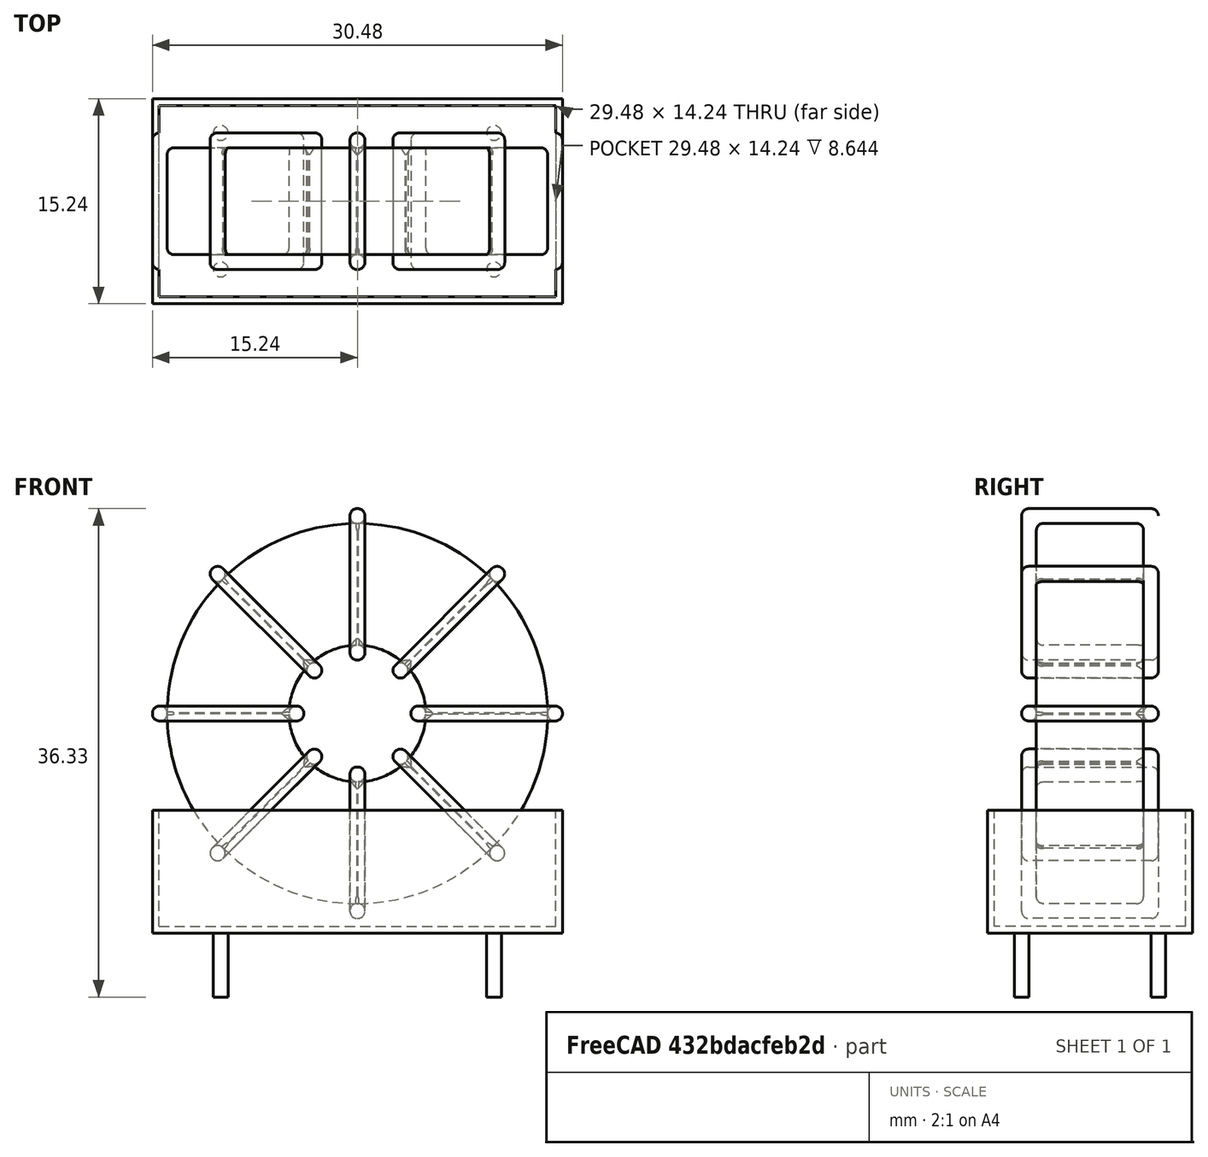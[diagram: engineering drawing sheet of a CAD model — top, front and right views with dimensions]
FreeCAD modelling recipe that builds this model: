
FCSTD DOCUMENT  (FreeCAD 0.16R6712 (Git))
Label: L_CommonMode_Toroid_Vertical_L30.5mm_W15.2mm_Px10.16mm_Py20.32mm_Bourns_8100
License: All rights reserved
LicenseURL: http://en.wikipedia.org/wiki/All_rights_reserved
objects: Sketcher::SketchObject×8, PartDesign::Pad×8, PartDesign::Fillet×5, Spreadsheet::Sheet×1, Part::MultiFuse×1
note: 30 computed .brp shape members not serialized (recipe doc carries the construction recipe); baked Part::Feature solids carry a one-line shape summary decoded from their .brp

FEATURE [Spreadsheet::Sheet] Spreadsheet  label="dimensions"
  cells = A1=Wx; B1(Wx)=30.48; C1(WW)=10.16; D1(iWx)=30.48; A2=Wy; B2(Wy)=10.16; D2(iWy)=15.24; A3=RM; B3(RMx)=10.16; C3(RMy)=20.32; A4=d_wire; B4(d_wire)=1.1; A5=H; B5(H)=31; A6=offsetx; B6(offsetx)=5.079999999999998
FEATURE [Sketcher::SketchObject] Sketch
  Placement = pos=(10.16,-5.08,0) rot=(1,0,0;1.5708rad)
  expr: Placement.Base.x = Spreadsheet.RMy / 2
  expr: Constraints[4] = Spreadsheet.WW / 2
  expr: Placement.Base.y = -Spreadsheet.RMx / 2
  expr: Constraints[0] = Spreadsheet.Wx / 2 - Spreadsheet.d_wire
  expr: Constraints[2] = Spreadsheet.Wx / 2 + Spreadsheet.d_wire + 0.5
  sketch-geometry (2):
    g0: Circle CenterX=0 CenterY=16.84 CenterZ=0 NormalX=0 NormalY=0 NormalZ=1 Radius=14.14
    g1: Circle CenterX=0 CenterY=16.84 CenterZ=0 NormalX=0 NormalY=0 NormalZ=1 Radius=5.08
  constraints (5):
    c: Radius(g0) = 14.14
    c: DistanceX(g-1,g0) = 0
    c: DistanceY(g-1,g0) = 16.84
    c: Coincident(g1,g0)
    c: Radius(g1) = 5.08
FEATURE [PartDesign::Pad] Pad
  Length = 7.96
  Length2 = 100
  Midplane = true
  Placement = pos=(10.16,-5.08,0) rot=(1,0,0;1.5708rad)
  Sketch = -> Sketch
  Type = 0
  expr: Length = Spreadsheet.Wy - 2 * Spreadsheet.d_wire
FEATURE [Sketcher::SketchObject] Sketch001
  Placement = pos=(0,0,0.75) rot=(0,0,1;0rad)
  expr: Constraints[4] = Spreadsheet.RMy
  expr: Constraints[2] = -Spreadsheet.RMx
  expr: Constraints[1] = Spreadsheet.d_wire / 2
  sketch-geometry (4):
    g0: Circle CenterX=0 CenterY=0 CenterZ=0 NormalX=0 NormalY=0 NormalZ=1 Radius=0.55
    g1: Circle CenterX=20.32 CenterY=-10.16 CenterZ=0 NormalX=0 NormalY=0 NormalZ=1 Radius=0.55
    g2: Circle CenterX=0 CenterY=-10.16 CenterZ=0 NormalX=0 NormalY=0 NormalZ=1 Radius=0.55
    g3: Circle CenterX=20.32 CenterY=0 CenterZ=0 NormalX=0 NormalY=0 NormalZ=1 Radius=0.55
  constraints (11):
    c: Equal(g0,g1)
    c: Radius(g0) = 0.55
    c: DistanceY(g-1,g1) = -10.16
    c: Coincident(g0,g-1)
    c: DistanceX(g-1,g1) = 20.32
    c: PointOnObject(g2,g-2)
    c: DistanceY(g-1,g3) = 0
    c: DistanceY(g2,g1) = 0
    c: DistanceX(g3,g1) = 0
    c: Equal(g3,g2)
    c: Equal(g2,g1)
FEATURE [PartDesign::Pad] Pad001
  Length = 5
  Length2 = 0
  Placement = pos=(0,0,0.75) rot=(0,0,1;0rad)
  Reversed = true
  Sketch = -> Sketch001
  Type = 0
FEATURE [PartDesign::Fillet] Fillet
  Base = -> Pad [Edge6,Edge3,Edge2]
  Placement = pos=(10.16,-5.08,0) rot=(1,0,0;1.5708rad)
  Radius = 0.5
FEATURE [Sketcher::SketchObject] Sketch003
  Placement = pos=(10.16,0,16.84) rot=(1,0,0;3.14159rad)
  expr: Placement.Base.x = Spreadsheet.RMy / 2
  expr: Constraints[18] = Spreadsheet.d_wire
  expr: Constraints[16] = Spreadsheet.d_wire
  expr: Constraints[19] = Spreadsheet.d_wire
  expr: Constraints[17] = Spreadsheet.d_wire
  expr: Placement.Base.y = -1 * (Spreadsheet.RMx - Spreadsheet.Wy) / 2
  expr: Constraints[21] = (Spreadsheet.Wx - Spreadsheet.WW) / 2 - Spreadsheet.d_wire
  expr: Constraints[22] = Spreadsheet.Wx / 2 - Spreadsheet.d_wire
  expr: Constraints[43] = Spreadsheet.d_wire
  expr: Constraints[48] = Spreadsheet.Wx - Spreadsheet.d_wire * 2
  expr: Constraints[49] = Spreadsheet.Wy
  expr: Placement.Base.z = Spreadsheet.Wx / 2 + Spreadsheet.d_wire + 0.5
  sketch-geometry (16):
    g0: LineSegment StartX=-3.98 StartY=0 StartZ=0 EndX=-15.24 EndY=0 EndZ=0
    g1: LineSegment StartX=-15.24 StartY=0 StartZ=0 EndX=-15.24 EndY=10.16 EndZ=0
    g2: LineSegment StartX=-15.24 StartY=10.16 StartZ=0 EndX=-3.98 EndY=10.16 EndZ=0
    g3: LineSegment StartX=-3.98 StartY=10.16 StartZ=0 EndX=-3.98 EndY=0 EndZ=0
    g4: LineSegment StartX=-14.14 StartY=9.06 StartZ=0 EndX=-5.08 EndY=9.06 EndZ=0
    g5: LineSegment StartX=-5.08 StartY=9.06 StartZ=0 EndX=-5.08 EndY=1.1 EndZ=0
    g6: LineSegment StartX=-5.08 StartY=1.1 StartZ=0 EndX=-14.14 EndY=1.1 EndZ=0
    g7: LineSegment StartX=-14.14 StartY=1.1 StartZ=0 EndX=-14.14 EndY=9.06 EndZ=0
    g8: LineSegment StartX=3.98 StartY=10.16 StartZ=0 EndX=15.24 EndY=10.16 EndZ=0
    g9: LineSegment StartX=15.24 StartY=10.16 StartZ=0 EndX=15.24 EndY=0 EndZ=0
    g10: LineSegment StartX=15.24 StartY=0 StartZ=0 EndX=3.98 EndY=0 EndZ=0
    g11: LineSegment StartX=3.98 StartY=0 StartZ=0 EndX=3.98 EndY=10.16 EndZ=0
    g12: LineSegment StartX=5.08 StartY=9.06 StartZ=0 EndX=14.14 EndY=9.06 EndZ=0
    g13: LineSegment StartX=14.14 StartY=9.06 StartZ=0 EndX=14.14 EndY=1.1 EndZ=0
    g14: LineSegment StartX=14.14 StartY=1.1 StartZ=0 EndX=5.08 EndY=1.1 EndZ=0
    g15: LineSegment StartX=5.08 StartY=1.1 StartZ=0 EndX=5.08 EndY=9.06 EndZ=0
  constraints (50):
    c: Horizontal(g0)
    c: Coincident(g1,g0)
    c: Vertical(g1)
    c: Coincident(g2,g1)
    c: Horizontal(g2)
    c: Coincident(g3,g2)
    c: Coincident(g3,g0)
    c: Vertical(g3)
    c: Coincident(g4,g5)
    c: Coincident(g5,g6)
    c: Coincident(g6,g7)
    c: Coincident(g7,g4)
    c: Horizontal(g4)
    c: Horizontal(g6)
    c: Vertical(g5)
    c: Vertical(g7)
    c: DistanceX(g1,g4) = 1.1
    c: DistanceY(g4,g1) = 1.1
    c: DistanceX(g5,g0) = 1.1
    c: DistanceY(g0,g5) = 1.1
    c: DistanceY(g-1,g0) = 0
    c: DistanceX(g6,g6) = 9.06
    c: DistanceX(g6,g-1) = 14.14
    c: Coincident(g8,g9)
    c: Coincident(g9,g10)
    c: Coincident(g10,g11)
    c: Coincident(g11,g8)
    c: Horizontal(g8)
    c: Horizontal(g10)
    c: Vertical(g9)
    c: Vertical(g11)
    c: Coincident(g12,g13)
    c: Coincident(g13,g14)
    c: Coincident(g14,g15)
    c: Coincident(g15,g12)
    c: Horizontal(g12)
    c: Horizontal(g14)
    c: Vertical(g13)
    c: Vertical(g15)
    c: DistanceY(g8,g2) = 0
    c: DistanceY(g10,g0) = 0
    c: DistanceY(g14,g5) = 0
    c: DistanceY(g12,g4) = 0
    c: DistanceX(g8,g12) = 1.1
    c: Equal(g8,g2)
    c: Equal(g12,g4)
    c: Equal(g9,g1)
    c: Equal(g13,g7)
    c: DistanceX(g4,g12) = 28.28
    c: DistanceY(g0,g1) = 10.16
FEATURE [PartDesign::Pad] Pad002
  Length = 1.1
  Length2 = 100
  Midplane = true
  Placement = pos=(10.16,0,16.84) rot=(1,0,0;3.14159rad)
  Sketch = -> Sketch003
  Type = 0
  expr: Length = Spreadsheet.d_wire
FEATURE [PartDesign::Fillet] Fillet001
  Base = -> Pad002 [Edge38,Edge41,Edge42,Edge43,Edge29,Edge32,Edge33,Edge34,Edge25,Edge35,Edge36,Edge13,Edge14,Edge15,Edge16,Edge17,Edge18,Edge19,Edge1,Edge2,Edge3,Edge4,Edge5,Edge6,Edge7,Edge37,Edge39,Edge40,Edge20,Edge23,Edge24,Edge21,Edge22,Edge8,Edge9,Edge10,Edge11,Edge12,Edge26,Edge27,+8 more]
  Placement = pos=(10.16,0,16.84) rot=(1,0,0;3.14159rad)
  Radius = 0.517
  expr: Radius = Spreadsheet.d_wire * 0.47
FEATURE [Sketcher::SketchObject] Sketch004
  Placement = pos=(10.16,0,16.84) rot=(0.92388,0,0.382683;3.14159rad)
  expr: Placement.Base.x = Spreadsheet.RMy / 2
  expr: Constraints[18] = Spreadsheet.d_wire
  expr: Constraints[16] = Spreadsheet.d_wire
  expr: Constraints[19] = Spreadsheet.d_wire
  expr: Constraints[17] = Spreadsheet.d_wire
  expr: Placement.Base.y = -1 * (Spreadsheet.RMx - Spreadsheet.Wy) / 2
  expr: Constraints[21] = (Spreadsheet.Wx - Spreadsheet.WW) / 2 - Spreadsheet.d_wire
  expr: Constraints[22] = Spreadsheet.Wx / 2 - Spreadsheet.d_wire
  expr: Constraints[43] = Spreadsheet.d_wire
  expr: Constraints[48] = Spreadsheet.Wx - 2 * Spreadsheet.d_wire
  expr: Constraints[49] = Spreadsheet.Wy
  expr: Placement.Base.z = Spreadsheet.Wx / 2 + Spreadsheet.d_wire + 0.5
  sketch-geometry (16):
    g0: LineSegment StartX=-3.98 StartY=0 StartZ=0 EndX=-15.24 EndY=0 EndZ=0
    g1: LineSegment StartX=-15.24 StartY=0 StartZ=0 EndX=-15.24 EndY=10.16 EndZ=0
    g2: LineSegment StartX=-15.24 StartY=10.16 StartZ=0 EndX=-3.98 EndY=10.16 EndZ=0
    g3: LineSegment StartX=-3.98 StartY=10.16 StartZ=0 EndX=-3.98 EndY=0 EndZ=0
    g4: LineSegment StartX=-14.14 StartY=9.06 StartZ=0 EndX=-5.08 EndY=9.06 EndZ=0
    g5: LineSegment StartX=-5.08 StartY=9.06 StartZ=0 EndX=-5.08 EndY=1.1 EndZ=0
    g6: LineSegment StartX=-5.08 StartY=1.1 StartZ=0 EndX=-14.14 EndY=1.1 EndZ=0
    g7: LineSegment StartX=-14.14 StartY=1.1 StartZ=0 EndX=-14.14 EndY=9.06 EndZ=0
    g8: LineSegment StartX=3.98 StartY=10.16 StartZ=0 EndX=15.24 EndY=10.16 EndZ=0
    g9: LineSegment StartX=15.24 StartY=10.16 StartZ=0 EndX=15.24 EndY=0 EndZ=0
    g10: LineSegment StartX=15.24 StartY=0 StartZ=0 EndX=3.98 EndY=0 EndZ=0
    g11: LineSegment StartX=3.98 StartY=0 StartZ=0 EndX=3.98 EndY=10.16 EndZ=0
    g12: LineSegment StartX=5.08 StartY=9.06 StartZ=0 EndX=14.14 EndY=9.06 EndZ=0
    g13: LineSegment StartX=14.14 StartY=9.06 StartZ=0 EndX=14.14 EndY=1.1 EndZ=0
    g14: LineSegment StartX=14.14 StartY=1.1 StartZ=0 EndX=5.08 EndY=1.1 EndZ=0
    g15: LineSegment StartX=5.08 StartY=1.1 StartZ=0 EndX=5.08 EndY=9.06 EndZ=0
  constraints (50):
    c: Horizontal(g0)
    c: Coincident(g1,g0)
    c: Vertical(g1)
    c: Coincident(g2,g1)
    c: Horizontal(g2)
    c: Coincident(g3,g2)
    c: Coincident(g3,g0)
    c: Vertical(g3)
    c: Coincident(g4,g5)
    c: Coincident(g5,g6)
    c: Coincident(g6,g7)
    c: Coincident(g7,g4)
    c: Horizontal(g4)
    c: Horizontal(g6)
    c: Vertical(g5)
    c: Vertical(g7)
    c: DistanceX(g1,g4) = 1.1
    c: DistanceY(g4,g1) = 1.1
    c: DistanceX(g5,g0) = 1.1
    c: DistanceY(g0,g5) = 1.1
    c: DistanceY(g-1,g0) = 0
    c: DistanceX(g6,g6) = 9.06
    c: DistanceX(g6,g-1) = 14.14
    c: Coincident(g8,g9)
    c: Coincident(g9,g10)
    c: Coincident(g10,g11)
    c: Coincident(g11,g8)
    c: Horizontal(g8)
    c: Horizontal(g10)
    c: Vertical(g9)
    c: Vertical(g11)
    c: Coincident(g12,g13)
    c: Coincident(g13,g14)
    c: Coincident(g14,g15)
    c: Coincident(g15,g12)
    c: Horizontal(g12)
    c: Horizontal(g14)
    c: Vertical(g13)
    c: Vertical(g15)
    c: DistanceY(g8,g2) = 0
    c: DistanceY(g10,g0) = 0
    c: DistanceY(g14,g5) = 0
    c: DistanceY(g12,g4) = 0
    c: DistanceX(g8,g12) = 1.1
    c: Equal(g8,g2)
    c: Equal(g12,g4)
    c: Equal(g9,g1)
    c: Equal(g13,g7)
    c: DistanceX(g4,g12) = 28.28
    c: DistanceY(g0,g1) = 10.16
FEATURE [PartDesign::Pad] Pad003
  Length = 1.1
  Length2 = 100
  Midplane = true
  Placement = pos=(10.16,0,16.84) rot=(0.92388,0,0.382683;3.14159rad)
  Sketch = -> Sketch004
  Type = 0
  expr: Length = Spreadsheet.d_wire
FEATURE [PartDesign::Fillet] Fillet002
  Base = -> Pad003 [Edge38,Edge41,Edge42,Edge43,Edge29,Edge32,Edge33,Edge34,Edge25,Edge35,Edge36,Edge13,Edge14,Edge15,Edge16,Edge17,Edge18,Edge19,Edge1,Edge2,Edge3,Edge4,Edge5,Edge6,Edge7,Edge37,Edge39,Edge40,Edge20,Edge23,Edge24,Edge21,Edge22,Edge8,Edge9,Edge10,Edge11,Edge12,Edge26,Edge27,+8 more]
  Placement = pos=(10.16,0,16.84) rot=(0.92388,0,0.382683;3.14159rad)
  Radius = 0.517
  expr: Radius = Spreadsheet.d_wire * 0.47
FEATURE [Sketcher::SketchObject] Sketch005
  Placement = pos=(10.16,0,16.84) rot=(0.92388,0,-0.382683;3.14159rad)
  expr: Placement.Base.x = Spreadsheet.RMy / 2
  expr: Constraints[18] = Spreadsheet.d_wire
  expr: Constraints[16] = Spreadsheet.d_wire
  expr: Constraints[19] = Spreadsheet.d_wire
  expr: Constraints[17] = Spreadsheet.d_wire
  expr: Placement.Base.y = -1 * (Spreadsheet.RMx - Spreadsheet.Wy) / 2
  expr: Constraints[21] = (Spreadsheet.Wx - Spreadsheet.WW) / 2 - Spreadsheet.d_wire
  expr: Constraints[22] = Spreadsheet.Wx / 2 - Spreadsheet.d_wire
  expr: Constraints[43] = Spreadsheet.d_wire
  expr: Constraints[48] = Spreadsheet.Wx - 2 * Spreadsheet.d_wire
  expr: Constraints[49] = Spreadsheet.Wy
  expr: Placement.Base.z = Spreadsheet.Wx / 2 + Spreadsheet.d_wire + 0.5
  sketch-geometry (16):
    g0: LineSegment StartX=-3.98 StartY=0 StartZ=0 EndX=-15.24 EndY=0 EndZ=0
    g1: LineSegment StartX=-15.24 StartY=0 StartZ=0 EndX=-15.24 EndY=10.16 EndZ=0
    g2: LineSegment StartX=-15.24 StartY=10.16 StartZ=0 EndX=-3.98 EndY=10.16 EndZ=0
    g3: LineSegment StartX=-3.98 StartY=10.16 StartZ=0 EndX=-3.98 EndY=0 EndZ=0
    g4: LineSegment StartX=-14.14 StartY=9.06 StartZ=0 EndX=-5.08 EndY=9.06 EndZ=0
    g5: LineSegment StartX=-5.08 StartY=9.06 StartZ=0 EndX=-5.08 EndY=1.1 EndZ=0
    g6: LineSegment StartX=-5.08 StartY=1.1 StartZ=0 EndX=-14.14 EndY=1.1 EndZ=0
    g7: LineSegment StartX=-14.14 StartY=1.1 StartZ=0 EndX=-14.14 EndY=9.06 EndZ=0
    g8: LineSegment StartX=3.98 StartY=10.16 StartZ=0 EndX=15.24 EndY=10.16 EndZ=0
    g9: LineSegment StartX=15.24 StartY=10.16 StartZ=0 EndX=15.24 EndY=0 EndZ=0
    g10: LineSegment StartX=15.24 StartY=0 StartZ=0 EndX=3.98 EndY=0 EndZ=0
    g11: LineSegment StartX=3.98 StartY=0 StartZ=0 EndX=3.98 EndY=10.16 EndZ=0
    g12: LineSegment StartX=5.08 StartY=9.06 StartZ=0 EndX=14.14 EndY=9.06 EndZ=0
    g13: LineSegment StartX=14.14 StartY=9.06 StartZ=0 EndX=14.14 EndY=1.1 EndZ=0
    g14: LineSegment StartX=14.14 StartY=1.1 StartZ=0 EndX=5.08 EndY=1.1 EndZ=0
    g15: LineSegment StartX=5.08 StartY=1.1 StartZ=0 EndX=5.08 EndY=9.06 EndZ=0
  constraints (50):
    c: Horizontal(g0)
    c: Coincident(g1,g0)
    c: Vertical(g1)
    c: Coincident(g2,g1)
    c: Horizontal(g2)
    c: Coincident(g3,g2)
    c: Coincident(g3,g0)
    c: Vertical(g3)
    c: Coincident(g4,g5)
    c: Coincident(g5,g6)
    c: Coincident(g6,g7)
    c: Coincident(g7,g4)
    c: Horizontal(g4)
    c: Horizontal(g6)
    c: Vertical(g5)
    c: Vertical(g7)
    c: DistanceX(g1,g4) = 1.1
    c: DistanceY(g4,g1) = 1.1
    c: DistanceX(g5,g0) = 1.1
    c: DistanceY(g0,g5) = 1.1
    c: DistanceY(g-1,g0) = 0
    c: DistanceX(g6,g6) = 9.06
    c: DistanceX(g6,g-1) = 14.14
    c: Coincident(g8,g9)
    c: Coincident(g9,g10)
    c: Coincident(g10,g11)
    c: Coincident(g11,g8)
    c: Horizontal(g8)
    c: Horizontal(g10)
    c: Vertical(g9)
    c: Vertical(g11)
    c: Coincident(g12,g13)
    c: Coincident(g13,g14)
    c: Coincident(g14,g15)
    c: Coincident(g15,g12)
    c: Horizontal(g12)
    c: Horizontal(g14)
    c: Vertical(g13)
    c: Vertical(g15)
    c: DistanceY(g8,g2) = 0
    c: DistanceY(g10,g0) = 0
    c: DistanceY(g14,g5) = 0
    c: DistanceY(g12,g4) = 0
    c: DistanceX(g8,g12) = 1.1
    c: Equal(g8,g2)
    c: Equal(g12,g4)
    c: Equal(g9,g1)
    c: Equal(g13,g7)
    c: DistanceX(g4,g12) = 28.28
    c: DistanceY(g0,g1) = 10.16
FEATURE [PartDesign::Pad] Pad004
  Length = 1.1
  Length2 = 100
  Midplane = true
  Placement = pos=(10.16,0,16.84) rot=(0.92388,0,-0.382683;3.14159rad)
  Sketch = -> Sketch005
  Type = 0
  expr: Length = Spreadsheet.d_wire
FEATURE [PartDesign::Fillet] Fillet003
  Base = -> Pad004 [Edge38,Edge41,Edge42,Edge43,Edge29,Edge32,Edge33,Edge34,Edge25,Edge35,Edge36,Edge13,Edge14,Edge15,Edge16,Edge17,Edge18,Edge19,Edge1,Edge2,Edge3,Edge4,Edge5,Edge6,Edge7,Edge37,Edge39,Edge40,Edge20,Edge23,Edge24,Edge21,Edge22,Edge8,Edge9,Edge10,Edge11,Edge12,Edge26,Edge27,+8 more]
  Placement = pos=(10.16,0,16.84) rot=(0.92388,0,-0.382683;3.14159rad)
  Radius = 0.517
  expr: Radius = Spreadsheet.d_wire * 0.47
FEATURE [Sketcher::SketchObject] Sketch006
  Placement = pos=(10.16,0,16.84) rot=(0.707107,0,0.707107;3.14159rad)
  expr: Placement.Base.x = Spreadsheet.RMy / 2
  expr: Constraints[18] = Spreadsheet.d_wire
  expr: Constraints[16] = Spreadsheet.d_wire
  expr: Constraints[19] = Spreadsheet.d_wire
  expr: Constraints[17] = Spreadsheet.d_wire
  expr: Placement.Base.y = -1 * (Spreadsheet.RMx - Spreadsheet.Wy) / 2
  expr: Constraints[21] = (Spreadsheet.Wx - Spreadsheet.WW) / 2 - Spreadsheet.d_wire
  expr: Constraints[22] = Spreadsheet.Wx / 2 - Spreadsheet.d_wire
  expr: Constraints[43] = Spreadsheet.d_wire
  expr: Constraints[48] = Spreadsheet.Wx - Spreadsheet.d_wire * 2
  expr: Constraints[49] = Spreadsheet.Wy
  expr: Placement.Base.z = Spreadsheet.Wx / 2 + Spreadsheet.d_wire + 0.5
  sketch-geometry (16):
    g0: LineSegment StartX=-3.98 StartY=0 StartZ=0 EndX=-15.24 EndY=0 EndZ=0
    g1: LineSegment StartX=-15.24 StartY=0 StartZ=0 EndX=-15.24 EndY=10.16 EndZ=0
    g2: LineSegment StartX=-15.24 StartY=10.16 StartZ=0 EndX=-3.98 EndY=10.16 EndZ=0
    g3: LineSegment StartX=-3.98 StartY=10.16 StartZ=0 EndX=-3.98 EndY=0 EndZ=0
    g4: LineSegment StartX=-14.14 StartY=9.06 StartZ=0 EndX=-5.08 EndY=9.06 EndZ=0
    g5: LineSegment StartX=-5.08 StartY=9.06 StartZ=0 EndX=-5.08 EndY=1.1 EndZ=0
    g6: LineSegment StartX=-5.08 StartY=1.1 StartZ=0 EndX=-14.14 EndY=1.1 EndZ=0
    g7: LineSegment StartX=-14.14 StartY=1.1 StartZ=0 EndX=-14.14 EndY=9.06 EndZ=0
    g8: LineSegment StartX=3.98 StartY=10.16 StartZ=0 EndX=15.24 EndY=10.16 EndZ=0
    g9: LineSegment StartX=15.24 StartY=10.16 StartZ=0 EndX=15.24 EndY=0 EndZ=0
    g10: LineSegment StartX=15.24 StartY=0 StartZ=0 EndX=3.98 EndY=0 EndZ=0
    g11: LineSegment StartX=3.98 StartY=0 StartZ=0 EndX=3.98 EndY=10.16 EndZ=0
    g12: LineSegment StartX=5.08 StartY=9.06 StartZ=0 EndX=14.14 EndY=9.06 EndZ=0
    g13: LineSegment StartX=14.14 StartY=9.06 StartZ=0 EndX=14.14 EndY=1.1 EndZ=0
    g14: LineSegment StartX=14.14 StartY=1.1 StartZ=0 EndX=5.08 EndY=1.1 EndZ=0
    g15: LineSegment StartX=5.08 StartY=1.1 StartZ=0 EndX=5.08 EndY=9.06 EndZ=0
  constraints (50):
    c: Horizontal(g0)
    c: Coincident(g1,g0)
    c: Vertical(g1)
    c: Coincident(g2,g1)
    c: Horizontal(g2)
    c: Coincident(g3,g2)
    c: Coincident(g3,g0)
    c: Vertical(g3)
    c: Coincident(g4,g5)
    c: Coincident(g5,g6)
    c: Coincident(g6,g7)
    c: Coincident(g7,g4)
    c: Horizontal(g4)
    c: Horizontal(g6)
    c: Vertical(g5)
    c: Vertical(g7)
    c: DistanceX(g1,g4) = 1.1
    c: DistanceY(g4,g1) = 1.1
    c: DistanceX(g5,g0) = 1.1
    c: DistanceY(g0,g5) = 1.1
    c: DistanceY(g-1,g0) = 0
    c: DistanceX(g6,g6) = 9.06
    c: DistanceX(g6,g-1) = 14.14
    c: Coincident(g8,g9)
    c: Coincident(g9,g10)
    c: Coincident(g10,g11)
    c: Coincident(g11,g8)
    c: Horizontal(g8)
    c: Horizontal(g10)
    c: Vertical(g9)
    c: Vertical(g11)
    c: Coincident(g12,g13)
    c: Coincident(g13,g14)
    c: Coincident(g14,g15)
    c: Coincident(g15,g12)
    c: Horizontal(g12)
    c: Horizontal(g14)
    c: Vertical(g13)
    c: Vertical(g15)
    c: DistanceY(g8,g2) = 0
    c: DistanceY(g10,g0) = 0
    c: DistanceY(g14,g5) = 0
    c: DistanceY(g12,g4) = 0
    c: DistanceX(g8,g12) = 1.1
    c: Equal(g8,g2)
    c: Equal(g12,g4)
    c: Equal(g9,g1)
    c: Equal(g13,g7)
    c: DistanceX(g4,g12) = 28.28
    c: DistanceY(g0,g1) = 10.16
FEATURE [PartDesign::Pad] Pad005
  Length = 1.1
  Length2 = 100
  Midplane = true
  Placement = pos=(10.16,0,16.84) rot=(0.707107,0,0.707107;3.14159rad)
  Sketch = -> Sketch006
  Type = 0
  expr: Length = Spreadsheet.d_wire
FEATURE [PartDesign::Fillet] Fillet004
  Base = -> Pad005 [Edge38,Edge41,Edge42,Edge43,Edge29,Edge32,Edge33,Edge34,Edge25,Edge35,Edge36,Edge13,Edge14,Edge15,Edge16,Edge17,Edge18,Edge19,Edge1,Edge2,Edge3,Edge4,Edge5,Edge6,Edge7,Edge37,Edge39,Edge40,Edge20,Edge23,Edge24,Edge21,Edge22,Edge8,Edge9,Edge10,Edge11,Edge12,Edge26,Edge27,+8 more]
  Placement = pos=(10.16,0,16.84) rot=(0.707107,0,0.707107;3.14159rad)
  Radius = 0.517
  expr: Radius = Spreadsheet.d_wire * 0.47
FEATURE [Sketcher::SketchObject] Sketch007
  Placement = pos=(10.16,0,0.5) rot=(0,0,1;0rad)
  expr: Placement.Base.x = Spreadsheet.RMy / 2
  expr: Placement.Base.z = 0.5
  expr: Constraints[11] = Spreadsheet.iWx / 2
  expr: Constraints[10] = (Spreadsheet.iWy - Spreadsheet.RMx) / 2
  expr: Constraints[9] = Spreadsheet.iWy
  expr: Constraints[8] = Spreadsheet.iWx
  sketch-geometry (4):
    g0: LineSegment StartX=-15.24 StartY=2.54 StartZ=0 EndX=15.24 EndY=2.54 EndZ=0
    g1: LineSegment StartX=15.24 StartY=2.54 StartZ=0 EndX=15.24 EndY=-12.7 EndZ=0
    g2: LineSegment StartX=15.24 StartY=-12.7 StartZ=0 EndX=-15.24 EndY=-12.7 EndZ=0
    g3: LineSegment StartX=-15.24 StartY=-12.7 StartZ=0 EndX=-15.24 EndY=2.54 EndZ=0
  constraints (12):
    c: Coincident(g0,g1)
    c: Coincident(g1,g2)
    c: Coincident(g2,g3)
    c: Coincident(g3,g0)
    c: Horizontal(g0)
    c: Horizontal(g2)
    c: Vertical(g1)
    c: Vertical(g3)
    c: DistanceX(g0,g0) = 30.48
    c: DistanceY(g3,g3) = 15.24
    c: DistanceY(g-1,g0) = 2.54
    c: DistanceX(g0,g-1) = 15.24
FEATURE [PartDesign::Pad] Pad006
  Length = 0.5
  Length2 = 100
  Placement = pos=(10.16,0,0.5) rot=(0,0,1;0rad)
  Sketch = -> Sketch007
  Type = 0
FEATURE [Sketcher::SketchObject] Sketch008
  Placement = pos=(10.16,0,0.5) rot=(0,0,1;0rad)
  expr: Placement.Base.x = Spreadsheet.RMy / 2
  expr: Constraints[8] = Spreadsheet.iWx
  expr: Constraints[9] = Spreadsheet.iWy
  expr: Constraints[10] = (Spreadsheet.iWy - Spreadsheet.RMx) / 2
  expr: Placement.Base.z = 0.5
  expr: Constraints[21] = 0.5
  expr: Constraints[11] = Spreadsheet.iWx / 2
  sketch-geometry (8):
    g0: LineSegment StartX=-15.24 StartY=2.54 StartZ=0 EndX=15.24 EndY=2.54 EndZ=0
    g1: LineSegment StartX=15.24 StartY=2.54 StartZ=0 EndX=15.24 EndY=-12.7 EndZ=0
    g2: LineSegment StartX=15.24 StartY=-12.7 StartZ=0 EndX=-15.24 EndY=-12.7 EndZ=0
    g3: LineSegment StartX=-15.24 StartY=-12.7 StartZ=0 EndX=-15.24 EndY=2.54 EndZ=0
    g4: LineSegment StartX=-14.74 StartY=2.04 StartZ=0 EndX=14.74 EndY=2.04 EndZ=0
    g5: LineSegment StartX=14.74 StartY=2.04 StartZ=0 EndX=14.74 EndY=-12.2 EndZ=0
    g6: LineSegment StartX=14.74 StartY=-12.2 StartZ=0 EndX=-14.74 EndY=-12.2 EndZ=0
    g7: LineSegment StartX=-14.74 StartY=-12.2 StartZ=0 EndX=-14.74 EndY=2.04 EndZ=0
  constraints (24):
    c: Coincident(g0,g1)
    c: Coincident(g1,g2)
    c: Coincident(g2,g3)
    c: Coincident(g3,g0)
    c: Horizontal(g0)
    c: Horizontal(g2)
    c: Vertical(g1)
    c: Vertical(g3)
    c: DistanceX(g0,g0) = 30.48
    c: DistanceY(g3,g3) = 15.24
    c: DistanceY(g-1,g0) = 2.54
    c: DistanceX(g0,g-1) = 15.24
    c: Coincident(g4,g5)
    c: Coincident(g5,g6)
    c: Coincident(g6,g7)
    c: Coincident(g7,g4)
    c: Horizontal(g4)
    c: Horizontal(g6)
    c: Vertical(g5)
    c: Vertical(g7)
    c: DistanceX(g5,g1) = 0.5
    c: DistanceY(g1,g5) = 0.5
    c: DistanceX(g0,g4) = 0.5
    c: DistanceY(g4,g0) = 0.5
FEATURE [PartDesign::Pad] Pad007
  Length = 9.144
  Length2 = 100
  Placement = pos=(10.16,0,0.5) rot=(0,0,1;0rad)
  Sketch = -> Sketch008
  Type = 0
  expr: Length = Spreadsheet.Wx * 0.3
FEATURE [Part::MultiFuse] Pad001_mp_cp  label="L_CommonMode_Toroid_Vertical_L30.5mm_W15.2mm_Px10.16mm_Py20.32mm_Bourns_8100"
  Shapes = -> [Pad001,Pad007,Pad006,Fillet002,Fillet004,Fillet,Fillet001,Fillet003]
